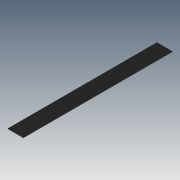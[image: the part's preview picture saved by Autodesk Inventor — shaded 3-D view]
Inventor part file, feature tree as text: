
AUTODESK INVENTOR PART (.ipt)
format: ipt  version: 2012 (Build 160160000, 160)  size: 66,048 bytes
history: native  units: in
note: dims shown in document units (in); Inventor stores cm internally (conversion verified against a paired STEP export)
features: extrude x1, sketch x1
ambient origin geometry x8: Origin, YZ Plane, XZ Plane, XY Plane, X Axis, Y Axis, Z Axis, Center Point
bodies: Solid1 (feature_tree)
feature tree (2):
  extrude  "Extrusion1"  Depth=0.0625in
  sketch  "Sketch1"  dims[d0=4.0in d1=0.0625in d2=38.0in d3=0.0in]
